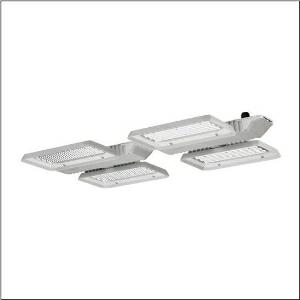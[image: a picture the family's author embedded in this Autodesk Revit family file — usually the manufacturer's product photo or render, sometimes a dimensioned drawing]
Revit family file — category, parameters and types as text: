
# Revit family: highbay_11_51hla2d24mca
name_source: partatom
category: Lighting Fixtures
units: mm (PartAtom-declared; Revit-internal decimal feet)

## family parameters
Cut with Voids When Loaded = No
Host = Face
Light Source = No
Part Type = Normal
Room Calculation Point = No
Round Connector Dimension = Use Diameter
Shared = No

## types (1)
- --- (1 x LED, 28800 lm, 162.4 W, 4000K)
    Apparent Load = 162 VA
    CIE Flux Codes = 89 96 99 100 100
    Color Rendering = 80
    Color Temperature = 4000K
    Default Elevation = 1800 mm
    Description = Highbay 11, LED high bay luminaire, primary light control with lens, of PMMA, light emission: direct distribution, primary light characteristic: symmetric, installation type: surface-mounted, suspended mounting, for 2x 2 x LED rated luminous flux: 28.800 lm, light colour: 840, colour temperature: 4000K, control gear: ECG DALI, with terminal, 5-pole, max. 2.5mm², mains connection: 230..240V, AC, 50/60Hz, rated input power: 162W, LED unit, of diecast aluminium, unplated, bead blasted, silver, length: 940 mm, width: 500 mm, height: 65mm, housing, of diecast aluminium, uncoated, bead blasted, silver, protection rating (complete): IP65, insulation class (complete): insulation class I (protective earthing), certification: CE, ENEC, VDE, protection symbol: D, impact resistance: IK08 with glass or PC cover, permissible ambient temperature for indoor applications: -35..+55°C, reducing of maximum allowable ambient temperature of 5°C with ceiling mounting, corresponds to IFS (International Featured Standards) requirements for safety and quality in the food industry, packaging unit: 1 piece
    Height = 95 mm
    Lamp = 1 x LED
    Lamp Light Flux = 28800 lm
    Lamp Power = 162.4 W
    Lamp count = 1
    Length = 939 mm
    Luminous efficacy = 177 lm/W
    Manufacturer = Siteco
    ModVariant = No
    Model = 51HLA2D24MCA
    Mounting Place = Ceiling
    Mounting Type = Pendant
    Number of Poles = 1
    OnlyDefault = Yes
    Power Factor = 1
    Product Name = Highbay 11
    Product group = LED high bay luminaire
    ProductGroupID = 903
    Protection Class = Protection class I
    Protection Degree = IP 65
    RLX_Detail_Level = 1
    RlxData = <blob elided: 96377 chars, md5=c4bd9d35>
    Socket = socket
    Standby Power = 0 W
    System Light Flux = 28800 lm
    System Power = 162 W
    Type Comments = factory setting: luminous flux: 100 % | dim-lin: 254 | 460 mA
    Type Image = l_1003428.jpg
    URL = http://relux.com
    VarID = @adj_140897
    Voltage = 0 V
    Weight = 0.00 kg
    Width = 501 mm

## geometry (parser evidence)
native form markers: Blend x4, Sweep x13
no freeform markers — native parametric forms only
